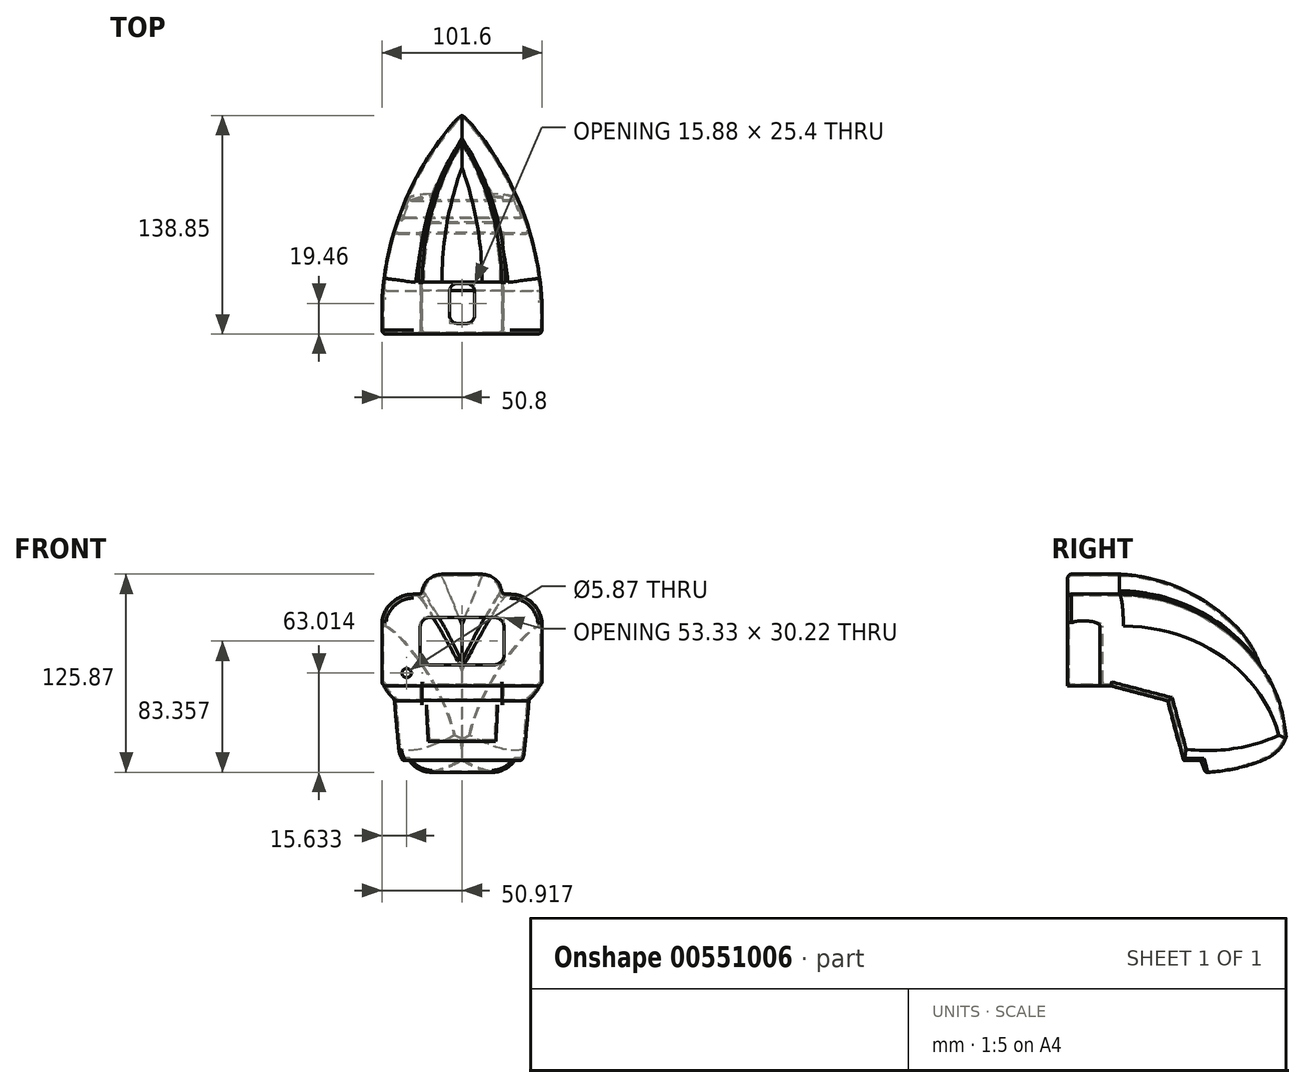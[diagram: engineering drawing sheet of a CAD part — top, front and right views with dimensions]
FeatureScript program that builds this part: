
annotation { "Feature Type Name" : "Feature", "Feature Type Description" : "" }
export const myFeature = defineFeature(function(context is Context, id is Id, definition is map)
    precondition{}
    {
        {
            var Q0;
            Q0=qCreatedBy(makeId("Right.planeOp"),FACE);
            var sketch = newSketch(context, id + "F0", { "sketchPlane" : qUnion([Q0])});
            skLineSegment(sketch, "E0.bottom", {"start": v(-27.47, 15.26) * mm, "end": v(97.38, 15.26) * mm});
            skLineSegment(sketch, "E0.top", {"start": v(-27.47, -90.97) * mm, "end": v(97.38, -90.97) * mm});
            skLineSegment(sketch, "E0.left", {"start": v(-27.47, 15.26) * mm, "end": v(-27.47, -90.97) * mm});
            skLineSegment(sketch, "E0.right", {"start": v(97.38, 15.26) * mm, "end": v(97.38, -90.97) * mm});
            skSolve(sketch);
        }
        {
            var Q0;
            Q0 = qSketchRegion(id + "F0", true);
            extrude(context, id + "F1", {"entities" : qUnion([Q0]), "depth" : 50.8 * mm, "offsetDistance" : 25.4 * mm});
        }
        {
            var Q0;
            Q0=makeQuery(id+"F1.opExtrude","CAP_FACE",FACE,{"disambiguationData":[OSD([sQuery(id+"F0.wireOp",EDGE,"E0.bottom"),sQuery(id+"F0.wireOp",EDGE,"E0.top"),sQuery(id+"F0.wireOp",EDGE,"E0.left"),sQuery(id+"F0.wireOp",EDGE,"E0.right")])],"isStart":false});
            var sketch = newSketch(context, id + "F2", { "sketchPlane" : qUnion([Q0])});
            skArc(sketch, "E1", {"start": v(97.38, -41.52) * mm, "mid": v(58.81, -1.33) * mm, "end": v(5.65, 15.26) * mm});
            skLineSegment(sketch, "E2", {"start": v(5.65, 15.26) * mm, "end": v(97.38, 15.26) * mm});
            skLineSegment(sketch, "E3", {"start": v(97.38, 15.26) * mm, "end": v(97.38, -41.52) * mm});
            skSolve(sketch);
        }
        {
            var Q0;
            Q0 = qSketchRegion(id + "F2", true);
            extrude(context, id + "F3", {"entities" : qUnion([Q0]), "operationType" : NewBodyOperationType.REMOVE, "endBound" : BoundingType.UP_TO_NEXT, "oppositeDirection" : true, "depth" : 25.4 * mm, "offsetDistance" : 25.4 * mm});
        }
        {
            var Q0;
            Q0=makeQuery(id+"F1.opExtrude","SWEPT_FACE",FACE,{"disambiguationData":[OSD([sQuery(id+"F0.wireOp",EDGE,"E0.bottom")])]});
            var sketch = newSketch(context, id + "F4", { "sketchPlane" : qUnion([Q0])});
            skLineSegment(sketch, "E4", {"start": v(25.4, -48.46) * mm, "end": v(25.4, 125.24) * mm, "construction": true});
            skPoint(sketch, "E4.startSnap0", {"position": v(25.4, -27.47) * mm});
            skArc(sketch, "E5", {"start": v(25.4, 97.46) * mm, "mid": v(6.47, 53.28) * mm, "end": v(0, 5.65) * mm});
            skArc(sketch, "E6.MirrorCS", {"start": v(25.4, 97.46) * mm, "mid": v(44.33, 53.28) * mm, "end": v(50.8, 5.65) * mm});
            skLineSegment(sketch, "E7", {"start": v(0, 5.65) * mm, "end": v(0, 98.9) * mm});
            skLineSegment(sketch, "E8", {"start": v(0, 98.9) * mm, "end": v(55.44, 98.9) * mm});
            skLineSegment(sketch, "E9", {"start": v(55.44, 98.9) * mm, "end": v(50.8, 5.65) * mm});
            skSolve(sketch);
        }
        {
            var Q0;
            Q0 = qSketchRegion(id + "F4", true);
            extrude(context, id + "F5", {"entities" : qUnion([Q0]), "operationType" : NewBodyOperationType.REMOVE, "endBound" : BoundingType.THROUGH_ALL, "oppositeDirection" : true, "depth" : 25.4 * mm, "offsetDistance" : 25.4 * mm});
        }
        {
            var Q0;
            Q0=makeQuery(id+"F5.boolean.opBoolean","INTERSECT",EDGE,{"derivedFrom":[makeQuery(id+"F3.boolean.opBoolean","COPY",FACE,{"derivedFrom":makeQuery(id+"F3.opExtrude","SWEPT_FACE",FACE,{"disambiguationData":[OSD([sQuery(id+"F2.wireOp",EDGE,"E1")])]})}),makeQuery(id+"F5.opExtrude","SWEPT_FACE",FACE,{"disambiguationData":[OSD([sQuery(id+"F4.wireOp",EDGE,"E5")])]})]});
            var Q1;
            Q1=makeQuery(id+"F5.boolean.opBoolean","INTERSECT",EDGE,{"derivedFrom":[makeQuery(id+"F3.boolean.opBoolean","COPY",FACE,{"derivedFrom":makeQuery(id+"F3.opExtrude","SWEPT_FACE",FACE,{"disambiguationData":[OSD([sQuery(id+"F2.wireOp",EDGE,"E1")])]})}),makeQuery(id+"F5.opExtrude","SWEPT_FACE",FACE,{"disambiguationData":[OSD([sQuery(id+"F4.wireOp",EDGE,"E6.MirrorCS")])]})]});
            fillet(context, id + "F6", {"entities" : qUnion([Q0, Q1]), "radius" : 12.7 * mm, "tangentPropagation" : true, "allowEdgeOverflow" : false});
        }
        {
            var Q0;
            Q0=makeQuery(id+"F1.opExtrude","CAP_FACE",FACE,{"disambiguationData":[OSD([sQuery(id+"F0.wireOp",EDGE,"E0.bottom"),sQuery(id+"F0.wireOp",EDGE,"E0.top"),sQuery(id+"F0.wireOp",EDGE,"E0.left"),sQuery(id+"F0.wireOp",EDGE,"E0.right")])],"isStart":true});
            var sketch = newSketch(context, id + "F7", { "sketchPlane" : qUnion([Q0])});
            skLineSegment(sketch, "E10", {"start": v(27.47, 2.56) * mm, "end": v(-5.31, 2.56) * mm});
            skArc(sketch, "E11", {"start": v(-5.31, 2.56) * mm, "mid": v(-70.73, -18.7) * mm, "end": v(-111.14, -74.37) * mm});
            skArc(sketch, "E12", {"start": v(-111.14, -74.37) * mm, "mid": v(-110.93, -89.35) * mm, "end": v(-101.3, -100.84) * mm});
            skArc(sketch, "E13", {"start": v(-101.3, -100.84) * mm, "mid": v(-81.11, -107.77) * mm, "end": v(-59.96, -110.67) * mm});
            skLineSegment(sketch, "E14", {"start": v(-59.96, -110.67) * mm, "end": v(-57.17, -102.96) * mm});
            skLineSegment(sketch, "E15", {"start": v(-57.17, -102.96) * mm, "end": v(-46.28, -102.96) * mm});
            skLineSegment(sketch, "E16", {"start": v(-46.28, -102.96) * mm, "end": v(-36.11, -65.2) * mm});
            skLineSegment(sketch, "E17", {"start": v(-36.11, -65.2) * mm, "end": v(0, -55.77) * mm});
            skLineSegment(sketch, "E18", {"start": v(0, -55.77) * mm, "end": v(27.47, -55.77) * mm});
            skLineSegment(sketch, "E19", {"start": v(27.47, -55.77) * mm, "end": v(27.47, 2.56) * mm});
            skSolve(sketch);
        }
        {
            var Q0;
            Q0 = qSketchRegion(id + "F7", true);
            extrude(context, id + "F8", {"entities" : qUnion([Q0]), "operationType" : NewBodyOperationType.ADD, "depth" : 25.4 * mm, "offsetDistance" : 25.4 * mm, "hasSecondDirection" : true, "secondDirectionOppositeDirection" : true, "secondDirectionDepth" : 76.2 * mm});
        }
        {
            var Q0;
            {var subQ2=sQuery(id+"F7.wireOp",EDGE,"E10");var subQ3=sQuery(id+"F0.wireOp",EDGE,"E0.bottom");Q0=makeQuery(id+"F8.boolean.opBoolean","SPLIT",FACE,{"disambiguationData":[TD([makeQuery(id+"F6.opFillet","BLEND_FACE",FACE,{"disambiguationData":[OSD([subQ3]),TDD([makeQuery(id+"F1.opExtrude","CAP_EDGE",EDGE,{"disambiguationData":[OSD([subQ3])],"isStart":false})])]})])],"derivedFrom":makeQuery(id+"F8.opExtrude","SWEPT_FACE",FACE,{"disambiguationData":[OSD([subQ2])]})});}
            var sketch = newSketch(context, id + "F9", { "sketchPlane" : qUnion([Q0])});
            skLineSegment(sketch, "E20", {"start": v(76.2, -27.53) * mm, "end": v(-25.5, -27.53) * mm, "construction": true});
            skLineSegment(sketch, "E21", {"start": v(25.35, -27.53) * mm, "end": v(25.35, 135.52) * mm, "construction": true});
            skLineSegment(sketch, "E22", {"start": v(76.2, -27.53) * mm, "end": v(84.37, 122.7) * mm});
            skLineSegment(sketch, "E23", {"start": v(84.37, 122.7) * mm, "end": v(25.35, 135.52) * mm});
            skLineSegment(sketch, "E24.MirrorCS", {"start": v(-25.5, -27.53) * mm, "end": v(-33.68, 122.7) * mm});
            skLineSegment(sketch, "E25.MirrorCS", {"start": v(-33.68, 122.7) * mm, "end": v(25.35, 135.52) * mm});
            skArc(sketch, "E26", {"start": v(76.2, -27.53) * mm, "mid": v(65.07, 47.74) * mm, "end": v(25.35, 112.63) * mm});
            skArc(sketch, "E27.MirrorCS", {"start": v(-25.5, -27.53) * mm, "mid": v(-14.37, 47.74) * mm, "end": v(25.35, 112.63) * mm});
            skSolve(sketch);
        }
        {
            var Q0;
            Q0 = qSketchRegion(id + "F9", true);
            extrude(context, id + "F10", {"entities" : qUnion([Q0]), "operationType" : NewBodyOperationType.REMOVE, "endBound" : BoundingType.THROUGH_ALL, "oppositeDirection" : true, "depth" : 25.4 * mm, "offsetDistance" : 25.4 * mm});
        }
        {
            var Q0;
            Q0=makeQuery(id+"F10.boolean.opBoolean","INTERSECT",EDGE,{"derivedFrom":[makeQuery(id+"F8.opExtrude","SWEPT_FACE",FACE,{"disambiguationData":[OSD([sQuery(id+"F7.wireOp",EDGE,"E11")])]}),makeQuery(id+"F10.opExtrude","SWEPT_FACE",FACE,{"disambiguationData":[OSD([sQuery(id+"F9.wireOp",EDGE,"E26")])]})]});
            var Q1;
            Q1=makeQuery(id+"F10.boolean.opBoolean","INTERSECT",EDGE,{"derivedFrom":[makeQuery(id+"F8.opExtrude","SWEPT_FACE",FACE,{"disambiguationData":[OSD([sQuery(id+"F7.wireOp",EDGE,"E11")])]}),makeQuery(id+"F10.opExtrude","SWEPT_FACE",FACE,{"disambiguationData":[OSD([sQuery(id+"F9.wireOp",EDGE,"E27.MirrorCS")])]})]});
            fillet(context, id + "F11", {"entities" : qUnion([Q0, Q1]), "radius" : 20.32 * mm, "tangentPropagation" : true, "allowEdgeOverflow" : false});
        }
        {
            var Q0;
            {var subQ0=sQuery(id+"F0.wireOp",EDGE,"E0.bottom");Q0=makeQuery(id+"F6.opFillet","BLEND_EDGE",EDGE,{"blendedFrom":[makeQuery(id+"F1.opExtrude","CAP_EDGE",EDGE,{"disambiguationData":[OSD([subQ0])],"isStart":true}),makeQuery(id+"F1.opExtrude","CAP_FACE",FACE,{"disambiguationData":[OSD([subQ0,sQuery(id+"F0.wireOp",EDGE,"E0.top"),sQuery(id+"F0.wireOp",EDGE,"E0.left"),sQuery(id+"F0.wireOp",EDGE,"E0.right")])],"isStart":true})],"blendedInto":[makeQuery(id+"F1.opExtrude","CAP_FACE",FACE,{"disambiguationData":[OSD([subQ0,sQuery(id+"F0.wireOp",EDGE,"E0.top"),sQuery(id+"F0.wireOp",EDGE,"E0.left"),sQuery(id+"F0.wireOp",EDGE,"E0.right")])],"isStart":true})]});}
            var Q1;
            {var subQ0=sQuery(id+"F0.wireOp",EDGE,"E0.bottom");Q1=makeQuery(id+"F6.opFillet","BLEND_EDGE",EDGE,{"blendedFrom":[makeQuery(id+"F1.opExtrude","CAP_EDGE",EDGE,{"disambiguationData":[OSD([subQ0])],"isStart":false}),makeQuery(id+"F1.opExtrude","CAP_FACE",FACE,{"disambiguationData":[OSD([subQ0,sQuery(id+"F0.wireOp",EDGE,"E0.top"),sQuery(id+"F0.wireOp",EDGE,"E0.left"),sQuery(id+"F0.wireOp",EDGE,"E0.right")])],"isStart":false})],"blendedInto":[makeQuery(id+"F1.opExtrude","CAP_FACE",FACE,{"disambiguationData":[OSD([subQ0,sQuery(id+"F0.wireOp",EDGE,"E0.top"),sQuery(id+"F0.wireOp",EDGE,"E0.left"),sQuery(id+"F0.wireOp",EDGE,"E0.right")])],"isStart":false})]});}
            var Q2;
            Q2=makeQuery(id+"F8.boolean.opBoolean","INTERSECT",EDGE,{"derivedFrom":[makeQuery(id+"F6.opFillet","BLEND_FACE",FACE,{"disambiguationData":[OSD([sQuery(id+"F2.wireOp",EDGE,"E1"),sQuery(id+"F4.wireOp",EDGE,"E6.MirrorCS")]),OD(1.0)]}),makeQuery(id+"F8.opExtrude","SWEPT_FACE",FACE,{"disambiguationData":[OSD([sQuery(id+"F7.wireOp",EDGE,"E11")])]})]});
            var Q3;
            Q3=makeQuery(id+"F8.boolean.opBoolean","INTERSECT",EDGE,{"derivedFrom":[makeQuery(id+"F6.opFillet","BLEND_FACE",FACE,{"disambiguationData":[OSD([sQuery(id+"F2.wireOp",EDGE,"E1"),sQuery(id+"F4.wireOp",EDGE,"E5")]),OD(1.0)]}),makeQuery(id+"F8.opExtrude","SWEPT_FACE",FACE,{"disambiguationData":[OSD([sQuery(id+"F7.wireOp",EDGE,"E11")])]})]});
            fillet(context, id + "F12", {"entities" : qUnion([Q0, Q1, Q2, Q3]), "radius" : 2.54 * mm, "tangentPropagation" : true, "allowEdgeOverflow" : false});
        }
        {
            var Q0;
            Q0=makeQuery(id+"F8.opExtrude","CAP_EDGE",EDGE,{"disambiguationData":[OSD([sQuery(id+"F7.wireOp",EDGE,"E19")])],"isStart":false});
            var Q1;
            Q1=makeQuery(id+"F11.opFillet","BLEND_EDGE",EDGE,{"blendedFrom":[makeQuery(id+"F10.boolean.opBoolean","COPY",EDGE,{"derivedFrom":makeQuery(id+"F10.opExtrude","CAP_EDGE",EDGE,{"disambiguationData":[OSD([sQuery(id+"F9.wireOp",EDGE,"E27.MirrorCS")])],"isStart":true})}),makeQuery(id+"F8.boolean.opBoolean","MERGE",FACE,{"derivedFrom":[makeQuery(id+"F1.opExtrude","SWEPT_FACE",FACE,{"disambiguationData":[OSD([sQuery(id+"F0.wireOp",EDGE,"E0.left")])]}),makeQuery(id+"F8.opExtrude","SWEPT_FACE",FACE,{"disambiguationData":[OSD([sQuery(id+"F7.wireOp",EDGE,"E19")])]})]})],"blendedInto":[makeQuery(id+"F8.boolean.opBoolean","MERGE",FACE,{"derivedFrom":[makeQuery(id+"F1.opExtrude","SWEPT_FACE",FACE,{"disambiguationData":[OSD([sQuery(id+"F0.wireOp",EDGE,"E0.left")])]}),makeQuery(id+"F8.opExtrude","SWEPT_FACE",FACE,{"disambiguationData":[OSD([sQuery(id+"F7.wireOp",EDGE,"E19")])]})]})]});
            var Q2;
            Q2=makeQuery(id+"F6.opFillet","BLEND_EDGE",EDGE,{"blendedFrom":[makeQuery(id+"F1.opExtrude","CAP_EDGE",EDGE,{"disambiguationData":[OSD([sQuery(id+"F0.wireOp",EDGE,"E0.bottom")])],"isStart":true}),makeQuery(id+"F1.opExtrude","SWEPT_FACE",FACE,{"disambiguationData":[OSD([sQuery(id+"F0.wireOp",EDGE,"E0.left")])]})],"blendedInto":[makeQuery(id+"F1.opExtrude","SWEPT_FACE",FACE,{"disambiguationData":[OSD([sQuery(id+"F0.wireOp",EDGE,"E0.left")])]})]});
            var Q3;
            {var subQ0=sQuery(id+"F0.wireOp",EDGE,"E0.left");var subQ1=sQuery(id+"F0.wireOp",EDGE,"E0.bottom");Q3=makeQuery(id+"F12.opFillet","BLEND_EDGE",EDGE,{"blendedFrom":[makeQuery(id+"F6.opFillet","BLEND_EDGE",EDGE,{"blendedFrom":[makeQuery(id+"F1.opExtrude","CAP_EDGE",EDGE,{"disambiguationData":[OSD([subQ1])],"isStart":true}),makeQuery(id+"F1.opExtrude","CAP_FACE",FACE,{"disambiguationData":[OSD([subQ1,sQuery(id+"F0.wireOp",EDGE,"E0.top"),subQ0,sQuery(id+"F0.wireOp",EDGE,"E0.right")])],"isStart":true})],"blendedInto":[makeQuery(id+"F1.opExtrude","CAP_FACE",FACE,{"disambiguationData":[OSD([subQ1,sQuery(id+"F0.wireOp",EDGE,"E0.top"),subQ0,sQuery(id+"F0.wireOp",EDGE,"E0.right")])],"isStart":true})]}),makeQuery(id+"F8.boolean.opBoolean","MERGE",FACE,{"derivedFrom":[makeQuery(id+"F1.opExtrude","SWEPT_FACE",FACE,{"disambiguationData":[OSD([subQ0])]}),makeQuery(id+"F8.opExtrude","SWEPT_FACE",FACE,{"disambiguationData":[OSD([sQuery(id+"F7.wireOp",EDGE,"E19")])]})]})],"blendedInto":[makeQuery(id+"F8.boolean.opBoolean","MERGE",FACE,{"derivedFrom":[makeQuery(id+"F1.opExtrude","SWEPT_FACE",FACE,{"disambiguationData":[OSD([subQ0])]}),makeQuery(id+"F8.opExtrude","SWEPT_FACE",FACE,{"disambiguationData":[OSD([sQuery(id+"F7.wireOp",EDGE,"E19")])]})]})]});}
            var Q4;
            {var subQ0=sQuery(id+"F7.wireOp",EDGE,"E10");var subQ1=sQuery(id+"F7.wireOp",EDGE,"E19");var subQ2=sQuery(id+"F0.wireOp",EDGE,"E0.bottom");Q4=makeQuery(id+"F8.boolean.opBoolean","SPLIT",EDGE,{"disambiguationData":[TD([makeQuery(id+"F6.opFillet","BLEND_FACE",FACE,{"disambiguationData":[OSD([subQ2]),TDD([makeQuery(id+"F1.opExtrude","CAP_EDGE",EDGE,{"disambiguationData":[OSD([subQ2])],"isStart":true})])]})])],"derivedFrom":makeQuery(id+"F8.opExtrude","SWEPT_EDGE",EDGE,{"disambiguationData":[OSD([subQ0,subQ1])]})});}
            var Q5;
            Q5=makeQuery(id+"F1.opExtrude","SWEPT_EDGE",EDGE,{"disambiguationData":[OSD([sQuery(id+"F0.wireOp",EDGE,"E0.bottom"),sQuery(id+"F0.wireOp",EDGE,"E0.left")])]});
            var Q6;
            Q6=makeQuery(id+"F6.opFillet","BLEND_EDGE",EDGE,{"blendedFrom":[makeQuery(id+"F1.opExtrude","CAP_EDGE",EDGE,{"disambiguationData":[OSD([sQuery(id+"F0.wireOp",EDGE,"E0.bottom")])],"isStart":false}),makeQuery(id+"F1.opExtrude","SWEPT_FACE",FACE,{"disambiguationData":[OSD([sQuery(id+"F0.wireOp",EDGE,"E0.left")])]})],"blendedInto":[makeQuery(id+"F1.opExtrude","SWEPT_FACE",FACE,{"disambiguationData":[OSD([sQuery(id+"F0.wireOp",EDGE,"E0.left")])]})]});
            var Q7;
            {var subQ0=sQuery(id+"F0.wireOp",EDGE,"E0.left");var subQ1=sQuery(id+"F0.wireOp",EDGE,"E0.bottom");Q7=makeQuery(id+"F12.opFillet","BLEND_EDGE",EDGE,{"blendedFrom":[makeQuery(id+"F6.opFillet","BLEND_EDGE",EDGE,{"blendedFrom":[makeQuery(id+"F1.opExtrude","CAP_EDGE",EDGE,{"disambiguationData":[OSD([subQ1])],"isStart":false}),makeQuery(id+"F1.opExtrude","CAP_FACE",FACE,{"disambiguationData":[OSD([subQ1,sQuery(id+"F0.wireOp",EDGE,"E0.top"),subQ0,sQuery(id+"F0.wireOp",EDGE,"E0.right")])],"isStart":false})],"blendedInto":[makeQuery(id+"F1.opExtrude","CAP_FACE",FACE,{"disambiguationData":[OSD([subQ1,sQuery(id+"F0.wireOp",EDGE,"E0.top"),subQ0,sQuery(id+"F0.wireOp",EDGE,"E0.right")])],"isStart":false})]}),makeQuery(id+"F8.boolean.opBoolean","MERGE",FACE,{"derivedFrom":[makeQuery(id+"F1.opExtrude","SWEPT_FACE",FACE,{"disambiguationData":[OSD([subQ0])]}),makeQuery(id+"F8.opExtrude","SWEPT_FACE",FACE,{"disambiguationData":[OSD([sQuery(id+"F7.wireOp",EDGE,"E19")])]})]})],"blendedInto":[makeQuery(id+"F8.boolean.opBoolean","MERGE",FACE,{"derivedFrom":[makeQuery(id+"F1.opExtrude","SWEPT_FACE",FACE,{"disambiguationData":[OSD([subQ0])]}),makeQuery(id+"F8.opExtrude","SWEPT_FACE",FACE,{"disambiguationData":[OSD([sQuery(id+"F7.wireOp",EDGE,"E19")])]})]})]});}
            var Q8;
            {var subQ0=sQuery(id+"F7.wireOp",EDGE,"E19");var subQ1=sQuery(id+"F7.wireOp",EDGE,"E10");var subQ2=sQuery(id+"F0.wireOp",EDGE,"E0.bottom");Q8=makeQuery(id+"F8.boolean.opBoolean","SPLIT",EDGE,{"disambiguationData":[TD([makeQuery(id+"F6.opFillet","BLEND_FACE",FACE,{"disambiguationData":[OSD([subQ2]),TDD([makeQuery(id+"F1.opExtrude","CAP_EDGE",EDGE,{"disambiguationData":[OSD([subQ2])],"isStart":false})])]})])],"derivedFrom":makeQuery(id+"F8.opExtrude","SWEPT_EDGE",EDGE,{"disambiguationData":[OSD([subQ1,subQ0])]})});}
            var Q9;
            Q9=makeQuery(id+"F8.opExtrude","CAP_EDGE",EDGE,{"disambiguationData":[OSD([sQuery(id+"F7.wireOp",EDGE,"E19")])],"isStart":true});
            var Q10;
            Q10=makeQuery(id+"F8.opExtrude","CAP_EDGE",EDGE,{"disambiguationData":[OSD([sQuery(id+"F7.wireOp",EDGE,"E18")])],"isStart":true});
            var Q11;
            {var subQ2=sQuery(id+"F7.wireOp",EDGE,"E17");Q11=makeQuery(id+"F10.boolean.opBoolean","INTERSECT",EDGE,{"derivedFrom":[makeQuery(id+"F8.boolean.opBoolean","SPLIT",FACE,{"disambiguationData":[TD([makeQuery(id+"F5.boolean.opBoolean","COPY",FACE,{"derivedFrom":makeQuery(id+"F5.opExtrude","SWEPT_FACE",FACE,{"disambiguationData":[OSD([sQuery(id+"F4.wireOp",EDGE,"E6.MirrorCS")])]})})])],"derivedFrom":makeQuery(id+"F8.opExtrude","SWEPT_FACE",FACE,{"disambiguationData":[OSD([subQ2])]})}),makeQuery(id+"F10.opExtrude","SWEPT_FACE",FACE,{"disambiguationData":[OSD([sQuery(id+"F9.wireOp",EDGE,"E26")])]})]});}
            var Q12;
            Q12=makeQuery(id+"F10.boolean.opBoolean","INTERSECT",EDGE,{"derivedFrom":[makeQuery(id+"F8.opExtrude","SWEPT_FACE",FACE,{"disambiguationData":[OSD([sQuery(id+"F7.wireOp",EDGE,"E16")])]}),makeQuery(id+"F10.opExtrude","SWEPT_FACE",FACE,{"disambiguationData":[OSD([sQuery(id+"F9.wireOp",EDGE,"E26")])]})]});
            var Q13;
            Q13=makeQuery(id+"F11.opFillet","BLEND_EDGE",EDGE,{"blendedFrom":[makeQuery(id+"F10.boolean.opBoolean","INTERSECT",EDGE,{"derivedFrom":[makeQuery(id+"F8.opExtrude","SWEPT_FACE",FACE,{"disambiguationData":[OSD([sQuery(id+"F7.wireOp",EDGE,"E13")])]}),makeQuery(id+"F10.opExtrude","SWEPT_FACE",FACE,{"disambiguationData":[OSD([sQuery(id+"F9.wireOp",EDGE,"E27.MirrorCS")])]})]}),makeQuery(id+"F8.opExtrude","SWEPT_FACE",FACE,{"disambiguationData":[OSD([sQuery(id+"F7.wireOp",EDGE,"E16")])]})],"blendedInto":[makeQuery(id+"F8.opExtrude","SWEPT_FACE",FACE,{"disambiguationData":[OSD([sQuery(id+"F7.wireOp",EDGE,"E16")])]})]});
            var Q14;
            {var subQ2=sQuery(id+"F7.wireOp",EDGE,"E17");Q14=makeQuery(id+"F10.boolean.opBoolean","INTERSECT",EDGE,{"derivedFrom":[makeQuery(id+"F8.boolean.opBoolean","SPLIT",FACE,{"disambiguationData":[TD([makeQuery(id+"F5.boolean.opBoolean","COPY",FACE,{"derivedFrom":makeQuery(id+"F5.opExtrude","SWEPT_FACE",FACE,{"disambiguationData":[OSD([sQuery(id+"F4.wireOp",EDGE,"E5")])]})})])],"derivedFrom":makeQuery(id+"F8.opExtrude","SWEPT_FACE",FACE,{"disambiguationData":[OSD([subQ2])]})}),makeQuery(id+"F10.opExtrude","SWEPT_FACE",FACE,{"disambiguationData":[OSD([sQuery(id+"F9.wireOp",EDGE,"E27.MirrorCS")])]})]});}
            var Q15;
            Q15=makeQuery(id+"F8.opExtrude","CAP_EDGE",EDGE,{"disambiguationData":[OSD([sQuery(id+"F7.wireOp",EDGE,"E18")])],"isStart":false});
            var Q16;
            {var subQ0=sQuery(id+"F7.wireOp",EDGE,"E18");var subQ1=sQuery(id+"F7.wireOp",EDGE,"E19");var subQ2=sQuery(id+"F0.wireOp",EDGE,"E0.left");Q16=makeQuery(id+"F8.boolean.opBoolean","SPLIT",EDGE,{"disambiguationData":[TD([makeQuery(id+"F1.opExtrude","CAP_FACE",FACE,{"disambiguationData":[OSD([sQuery(id+"F0.wireOp",EDGE,"E0.bottom"),sQuery(id+"F0.wireOp",EDGE,"E0.top"),subQ2,sQuery(id+"F0.wireOp",EDGE,"E0.right")])],"isStart":true})])],"derivedFrom":makeQuery(id+"F8.opExtrude","SWEPT_EDGE",EDGE,{"disambiguationData":[OSD([subQ2,subQ0,subQ1])]})});}
            var Q17;
            {var subQ0=sQuery(id+"F7.wireOp",EDGE,"E19");var subQ1=sQuery(id+"F7.wireOp",EDGE,"E18");var subQ2=sQuery(id+"F0.wireOp",EDGE,"E0.left");Q17=makeQuery(id+"F8.boolean.opBoolean","SPLIT",EDGE,{"disambiguationData":[TD([makeQuery(id+"F1.opExtrude","CAP_FACE",FACE,{"disambiguationData":[OSD([sQuery(id+"F0.wireOp",EDGE,"E0.bottom"),sQuery(id+"F0.wireOp",EDGE,"E0.top"),subQ2,sQuery(id+"F0.wireOp",EDGE,"E0.right")])],"isStart":false})])],"derivedFrom":makeQuery(id+"F8.opExtrude","SWEPT_EDGE",EDGE,{"disambiguationData":[OSD([subQ2,subQ1,subQ0])]})});}
            fillet(context, id + "F13", {"entities" : qUnion([Q0, Q1, Q2, Q3, Q4, Q5, Q6, Q7, Q8, Q9, Q10, Q11, Q12, Q13, Q14, Q15, Q16, Q17]), "radius" : 2.54 * mm, "tangentPropagation" : true, "allowEdgeOverflow" : false});
        }
        {
            var Q0;
            Q0=qCreatedBy(makeId("Right.planeOp"),FACE);
            var sketch = newSketch(context, id + "F14", { "sketchPlane" : qUnion([Q0])});
            skLineSegment(sketch, "E28", {"start": v(-27.57, -55.6) * mm, "end": v(0, -55.6) * mm});
            skLineSegment(sketch, "E29", {"start": v(0, -55.6) * mm, "end": v(36.1, -65.1) * mm});
            skLineSegment(sketch, "E30", {"start": v(36.1, -65.1) * mm, "end": v(43.87, -94.88) * mm});
            skLineSegment(sketch, "E31", {"start": v(43.87, -94.88) * mm, "end": v(-29.95, -94.88) * mm});
            skLineSegment(sketch, "E32", {"start": v(-29.95, -94.88) * mm, "end": v(-29.95, -54.95) * mm});
            skLineSegment(sketch, "E33", {"start": v(-29.95, -54.95) * mm, "end": v(-27.57, -55.6) * mm});
            skSolve(sketch);
        }
        {
            var Q0;
            Q0 = qSketchRegion(id + "F14", true);
            var Q1;
            Q1=makeQuery(id+"F1.opExtrude","CAP_FACE",FACE,{"disambiguationData":[OSD([sQuery(id+"F0.wireOp",EDGE,"E0.bottom"),sQuery(id+"F0.wireOp",EDGE,"E0.top"),sQuery(id+"F0.wireOp",EDGE,"E0.left"),sQuery(id+"F0.wireOp",EDGE,"E0.right")])],"isStart":false});
            extrude(context, id + "F15", {"entities" : qUnion([Q0]), "operationType" : NewBodyOperationType.REMOVE, "endBound" : BoundingType.UP_TO_SURFACE, "depth" : 25.4 * mm, "endBoundEntityFace" : qUnion([Q1]), "offsetDistance" : 25.4 * mm});
        }
        {
            var Q0;
            Q0=makeQuery(id+"F8.opExtrude","SWEPT_EDGE",EDGE,{"disambiguationData":[OSD([sQuery(id+"F7.wireOp",EDGE,"E13"),sQuery(id+"F7.wireOp",EDGE,"E14")])]});
            var Q1;
            Q1=makeQuery(id+"F11.opFillet","BLEND_EDGE",EDGE,{"blendedFrom":[makeQuery(id+"F10.boolean.opBoolean","INTERSECT",EDGE,{"derivedFrom":[makeQuery(id+"F8.opExtrude","SWEPT_FACE",FACE,{"disambiguationData":[OSD([sQuery(id+"F7.wireOp",EDGE,"E13")])]}),makeQuery(id+"F10.opExtrude","SWEPT_FACE",FACE,{"disambiguationData":[OSD([sQuery(id+"F9.wireOp",EDGE,"E26")])]})]}),makeQuery(id+"F8.opExtrude","SWEPT_FACE",FACE,{"disambiguationData":[OSD([sQuery(id+"F7.wireOp",EDGE,"E15")])]})],"blendedInto":[makeQuery(id+"F8.opExtrude","SWEPT_FACE",FACE,{"disambiguationData":[OSD([sQuery(id+"F7.wireOp",EDGE,"E15")])]})]});
            fillet(context, id + "F16", {"entities" : qUnion([Q0, Q1]), "radius" : 1.9 * mm, "tangentPropagation" : true, "allowEdgeOverflow" : false});
        }
        {
            var Q0;
            Q0=makeQuery(id+"F10.boolean.opBoolean","INTERSECT",EDGE,{"derivedFrom":[makeQuery(id+"F8.opExtrude","SWEPT_FACE",FACE,{"disambiguationData":[OSD([sQuery(id+"F7.wireOp",EDGE,"E13")])]}),makeQuery(id+"F10.opExtrude","SWEPT_FACE",FACE,{"disambiguationData":[OSD([sQuery(id+"F9.wireOp",EDGE,"E26")])]})]});
            var Q1;
            Q1=makeQuery(id+"F10.boolean.opBoolean","INTERSECT",EDGE,{"derivedFrom":[makeQuery(id+"F8.opExtrude","SWEPT_FACE",FACE,{"disambiguationData":[OSD([sQuery(id+"F7.wireOp",EDGE,"E13")])]}),makeQuery(id+"F10.opExtrude","SWEPT_FACE",FACE,{"disambiguationData":[OSD([sQuery(id+"F9.wireOp",EDGE,"E27.MirrorCS")])]})]});
            fillet(context, id + "F17", {"entities" : qUnion([Q0, Q1]), "radius" : 13.97 * mm, "tangentPropagation" : true, "allowEdgeOverflow" : false});
        }
        {
            var Q0;
            Q0=makeQuery(id+"F10.boolean.opBoolean","INTERSECT",EDGE,{"derivedFrom":[makeQuery(id+"F8.opExtrude","SWEPT_FACE",FACE,{"disambiguationData":[OSD([sQuery(id+"F7.wireOp",EDGE,"E16")])]}),makeQuery(id+"F10.opExtrude","SWEPT_FACE",FACE,{"disambiguationData":[OSD([sQuery(id+"F9.wireOp",EDGE,"E27.MirrorCS")])]})]});
            var Q1;
            {var subQ0=makeQuery(id+"F8.opExtrude","SWEPT_FACE",FACE,{"disambiguationData":[OSD([sQuery(id+"F7.wireOp",EDGE,"E16")])]});Q1=makeQuery(id+"F13.opFillet","BLEND_EDGE",EDGE,{"blendedFrom":[makeQuery(id+"F10.boolean.opBoolean","INTERSECT",EDGE,{"derivedFrom":[subQ0,makeQuery(id+"F10.opExtrude","SWEPT_FACE",FACE,{"disambiguationData":[OSD([sQuery(id+"F9.wireOp",EDGE,"E26")])]})]}),subQ0],"blendedInto":[subQ0]});}
            var Q2;
            Q2=makeQuery(id+"F17.opFillet","BLEND_EDGE",EDGE,{"blendedFrom":[makeQuery(id+"F10.boolean.opBoolean","INTERSECT",EDGE,{"derivedFrom":[makeQuery(id+"F8.opExtrude","SWEPT_FACE",FACE,{"disambiguationData":[OSD([sQuery(id+"F7.wireOp",EDGE,"E13")])]}),makeQuery(id+"F10.opExtrude","SWEPT_FACE",FACE,{"disambiguationData":[OSD([sQuery(id+"F9.wireOp",EDGE,"E27.MirrorCS")])]})]}),makeQuery(id+"F8.opExtrude","SWEPT_FACE",FACE,{"disambiguationData":[OSD([sQuery(id+"F7.wireOp",EDGE,"E14")])]})],"blendedInto":[makeQuery(id+"F8.opExtrude","SWEPT_FACE",FACE,{"disambiguationData":[OSD([sQuery(id+"F7.wireOp",EDGE,"E14")])]})]});
            var Q3;
            Q3=makeQuery(id+"F17.opFillet","BLEND_EDGE",EDGE,{"blendedFrom":[makeQuery(id+"F10.boolean.opBoolean","INTERSECT",EDGE,{"derivedFrom":[makeQuery(id+"F8.opExtrude","SWEPT_FACE",FACE,{"disambiguationData":[OSD([sQuery(id+"F7.wireOp",EDGE,"E13")])]}),makeQuery(id+"F10.opExtrude","SWEPT_FACE",FACE,{"disambiguationData":[OSD([sQuery(id+"F9.wireOp",EDGE,"E27.MirrorCS")])]})]}),makeQuery(id+"F8.opExtrude","SWEPT_FACE",FACE,{"disambiguationData":[OSD([sQuery(id+"F7.wireOp",EDGE,"E15")])]})],"blendedInto":[makeQuery(id+"F8.opExtrude","SWEPT_FACE",FACE,{"disambiguationData":[OSD([sQuery(id+"F7.wireOp",EDGE,"E15")])]})]});
            var Q4;
            Q4=makeQuery(id+"F17.opFillet","BLEND_EDGE",EDGE,{"blendedFrom":[makeQuery(id+"F10.boolean.opBoolean","INTERSECT",EDGE,{"derivedFrom":[makeQuery(id+"F8.opExtrude","SWEPT_FACE",FACE,{"disambiguationData":[OSD([sQuery(id+"F7.wireOp",EDGE,"E13")])]}),makeQuery(id+"F10.opExtrude","SWEPT_FACE",FACE,{"disambiguationData":[OSD([sQuery(id+"F9.wireOp",EDGE,"E26")])]})]}),makeQuery(id+"F8.opExtrude","SWEPT_FACE",FACE,{"disambiguationData":[OSD([sQuery(id+"F7.wireOp",EDGE,"E15")])]})],"blendedInto":[makeQuery(id+"F8.opExtrude","SWEPT_FACE",FACE,{"disambiguationData":[OSD([sQuery(id+"F7.wireOp",EDGE,"E15")])]})]});
            var Q5;
            Q5=makeQuery(id+"F17.opFillet","BLEND_EDGE",EDGE,{"blendedFrom":[makeQuery(id+"F10.boolean.opBoolean","INTERSECT",EDGE,{"derivedFrom":[makeQuery(id+"F8.opExtrude","SWEPT_FACE",FACE,{"disambiguationData":[OSD([sQuery(id+"F7.wireOp",EDGE,"E13")])]}),makeQuery(id+"F10.opExtrude","SWEPT_FACE",FACE,{"disambiguationData":[OSD([sQuery(id+"F9.wireOp",EDGE,"E26")])]})]}),makeQuery(id+"F8.opExtrude","SWEPT_FACE",FACE,{"disambiguationData":[OSD([sQuery(id+"F7.wireOp",EDGE,"E14")])]})],"blendedInto":[makeQuery(id+"F8.opExtrude","SWEPT_FACE",FACE,{"disambiguationData":[OSD([sQuery(id+"F7.wireOp",EDGE,"E14")])]})]});
            fillet(context, id + "F18", {"entities" : qUnion([Q0, Q1, Q2, Q3, Q4, Q5]), "radius" : 1.9 * mm, "tangentPropagation" : true, "allowEdgeOverflow" : false});
        }
        {
            var Q0;
            Q0=makeQuery(id+"F8.boolean.opBoolean","MERGE",FACE,{"derivedFrom":[makeQuery(id+"F1.opExtrude","SWEPT_FACE",FACE,{"disambiguationData":[OSD([sQuery(id+"F0.wireOp",EDGE,"E0.left")])]}),makeQuery(id+"F8.opExtrude","SWEPT_FACE",FACE,{"disambiguationData":[OSD([sQuery(id+"F7.wireOp",EDGE,"E19")])]})]});
            var sketch = newSketch(context, id + "F19", { "sketchPlane" : qUnion([Q0])});
            skLineSegment(sketch, "E34", {"start": v(25.4, -55.6) * mm, "end": v(25.4, -55.6) * mm});
            skPoint(sketch, "E34.endSnap0", {"position": v(25.4, 12.72) * mm});
            skLineSegment(sketch, "E35.bottom", {"start": v(45.83, -12.14) * mm, "end": v(5.2, -12.14) * mm});
            skLineSegment(sketch, "E35.top", {"start": v(45.83, -42.36) * mm, "end": v(5.2, -42.36) * mm});
            skLineSegment(sketch, "E35.left", {"start": v(52.18, -18.5) * mm, "end": v(52.18, -36.01) * mm});
            skLineSegment(sketch, "E35.right", {"start": v(-1.15, -18.5) * mm, "end": v(-1.15, -36.01) * mm});
            skPoint(sketch, "E35.middle", {"position": v(25.52, -27.25) * mm});
            skPoint(sketch, "E36.visualSharp", {"position": v(-1.15, -12.14) * mm});
            skArc(sketch, "E36.filletArc", {"start": v(5.2, -12.14) * mm, "mid": v(0.7, -14) * mm, "end": v(-1.15, -18.5) * mm});
            skPoint(sketch, "E37.visualSharp", {"position": v(52.18, -12.14) * mm});
            skArc(sketch, "E37.filletArc", {"start": v(52.18, -18.5) * mm, "mid": v(50.32, -14) * mm, "end": v(45.83, -12.14) * mm});
            skPoint(sketch, "E38.visualSharp", {"position": v(52.18, -42.36) * mm});
            skArc(sketch, "E38.filletArc", {"start": v(45.83, -42.36) * mm, "mid": v(50.32, -40.5) * mm, "end": v(52.18, -36.01) * mm});
            skPoint(sketch, "E39.visualSharp", {"position": v(-1.15, -42.36) * mm});
            skArc(sketch, "E39.filletArc", {"start": v(-1.15, -36.01) * mm, "mid": v(0.7, -40.5) * mm, "end": v(5.2, -42.36) * mm});
            skSolve(sketch);
        }
        {
            var Q0;
            Q0 = qSketchRegion(id + "F19", true);
            extrude(context, id + "F20", {"entities" : qUnion([Q0]), "operationType" : NewBodyOperationType.REMOVE, "oppositeDirection" : true, "depth" : 0.95 * mm, "offsetDistance" : 25.4 * mm});
        }
        {
            var Q0;
            Q0=makeQuery(id+"F20.boolean.opBoolean","COPY",FACE,{"derivedFrom":makeQuery(id+"F20.opExtrude","CAP_FACE",FACE,{"disambiguationData":[OSD([sQuery(id+"F19.wireOp",EDGE,"E35.bottom"),sQuery(id+"F19.wireOp",EDGE,"E35.top"),sQuery(id+"F19.wireOp",EDGE,"E35.left"),sQuery(id+"F19.wireOp",EDGE,"E35.right"),sQuery(id+"F19.wireOp",EDGE,"E36.filletArc"),sQuery(id+"F19.wireOp",EDGE,"E37.filletArc"),sQuery(id+"F19.wireOp",EDGE,"E38.filletArc"),sQuery(id+"F19.wireOp",EDGE,"E39.filletArc")])],"isStart":false})});
            shell(context, id + "F21", {"entities" : qUnion([Q0]), "thickness" : 0.95 * mm});
        }
        {
            var Q0;
            Q0=makeQuery(id+"F8.boolean.opBoolean","MERGE",FACE,{"derivedFrom":[makeQuery(id+"F1.opExtrude","SWEPT_FACE",FACE,{"disambiguationData":[OSD([sQuery(id+"F0.wireOp",EDGE,"E0.left")])]}),makeQuery(id+"F8.opExtrude","SWEPT_FACE",FACE,{"disambiguationData":[OSD([sQuery(id+"F7.wireOp",EDGE,"E19")])]})]});
            var sketch = newSketch(context, id + "F22", { "sketchPlane" : qUnion([Q0])});
            skCircle(sketch, "E40", {"center": v(-9.77, -47.6) * mm, "radius": 2.94 * mm});
            skSolve(sketch);
        }
        {
            var Q0;
            Q0 = qSketchRegion(id + "F22", true);
            extrude(context, id + "F23", {"entities" : qUnion([Q0]), "operationType" : NewBodyOperationType.REMOVE, "endBound" : BoundingType.UP_TO_NEXT, "oppositeDirection" : true, "depth" : 25.4 * mm, "offsetDistance" : 25.4 * mm});
        }
        {
            var Q0;
            Q0=makeQuery(id+"F1.opExtrude","SWEPT_FACE",FACE,{"disambiguationData":[OSD([sQuery(id+"F0.wireOp",EDGE,"E0.bottom")])]});
            var sketch = newSketch(context, id + "F24", { "sketchPlane" : qUnion([Q0])});
            skLineSegment(sketch, "E41.bottom", {"start": v(28.26, -20.7) * mm, "end": v(22.54, -20.7) * mm});
            skLineSegment(sketch, "E41.top", {"start": v(28.26, 4.7) * mm, "end": v(22.54, 4.7) * mm});
            skLineSegment(sketch, "E41.left", {"start": v(33.34, -15.63) * mm, "end": v(33.34, -0.39) * mm});
            skLineSegment(sketch, "E41.right", {"start": v(17.46, -15.63) * mm, "end": v(17.46, -0.39) * mm});
            skPoint(sketch, "E41.middle", {"position": v(25.4, -8) * mm});
            skPoint(sketch, "E41.middle.positionSnap0", {"position": v(25.4, -24.93) * mm});
            skPoint(sketch, "E41.centerSnap0", {"position": v(25.4, -24.93) * mm});
            skPoint(sketch, "E42.visualSharp", {"position": v(17.46, 4.7) * mm});
            skArc(sketch, "E42.filletArc", {"start": v(22.54, 4.7) * mm, "mid": v(18.95, 3.2) * mm, "end": v(17.46, -0.39) * mm});
            skPoint(sketch, "E43.visualSharp", {"position": v(33.34, 4.7) * mm});
            skArc(sketch, "E43.filletArc", {"start": v(33.34, -0.39) * mm, "mid": v(31.85, 3.2) * mm, "end": v(28.26, 4.7) * mm});
            skPoint(sketch, "E44.visualSharp", {"position": v(17.46, -20.7) * mm});
            skArc(sketch, "E44.filletArc", {"start": v(17.46, -15.63) * mm, "mid": v(18.95, -19.22) * mm, "end": v(22.54, -20.7) * mm});
            skPoint(sketch, "E45.visualSharp", {"position": v(33.34, -20.7) * mm});
            skArc(sketch, "E45.filletArc", {"start": v(28.26, -20.7) * mm, "mid": v(31.85, -19.22) * mm, "end": v(33.34, -15.63) * mm});
            skSolve(sketch);
        }
        {
            var Q0;
            Q0 = qSketchRegion(id + "F24", true);
            extrude(context, id + "F25", {"entities" : qUnion([Q0]), "operationType" : NewBodyOperationType.REMOVE, "endBound" : BoundingType.UP_TO_NEXT, "oppositeDirection" : true, "depth" : 25.4 * mm, "offsetDistance" : 25.4 * mm});
        }
    });
